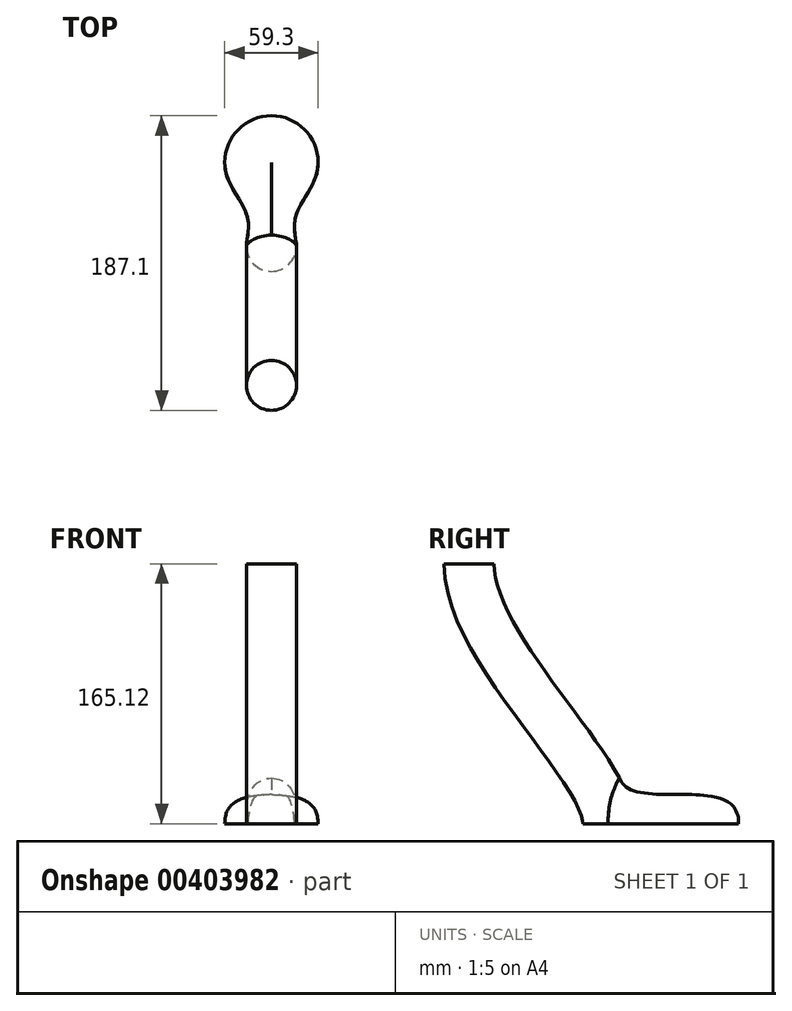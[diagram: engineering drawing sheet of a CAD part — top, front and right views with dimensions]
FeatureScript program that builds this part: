
annotation { "Feature Type Name" : "Feature", "Feature Type Description" : "" }
export const myFeature = defineFeature(function(context is Context, id is Id, definition is map)
    precondition{}
    {
        {
            var Q0;
            Q0=qCreatedBy(makeId("Top.planeOp"),FACE);
            var sketch = newSketch(context, id + "F0", { "sketchPlane" : qUnion([Q0])});
            skArc(sketch, "E0", {"start": v(0, -29.65) * mm, "mid": v(29.65, 0) * mm, "end": v(0, 29.65) * mm});
            skArc(sketch, "E1", {"start": v(0, -64.45) * mm, "mid": v(11.11, -53.34) * mm, "end": v(0, -42.23) * mm});
            skArc(sketch, "E2", {"start": v(0, -69.22) * mm, "mid": v(15.88, -53.34) * mm, "end": v(0, -37.46) * mm});
            skArc(sketch, "E3", {"start": v(0, -15.88) * mm, "mid": v(15.88, 0) * mm, "end": v(0, 15.88) * mm});
            skLineSegment(sketch, "E4", {"start": v(0, 29.65) * mm, "end": v(0, -69.22) * mm});
            skSolve(sketch);
        }
        {
            var Q0;
            Q0=qCreatedBy(makeId("Right.planeOp"),FACE);
            var sketch = newSketch(context, id + "F1", { "sketchPlane" : qUnion([Q0])});
            skLineSegment(sketch, "E5", {"start": v(0, 0) * mm, "end": v(0, 18.54) * mm});
            skPoint(sketch, "E6.0", {"position": v(29.65, 0) * mm});
            skLineSegment(sketch, "E7", {"start": v(0, 0) * mm, "end": v(29.65, 0) * mm});
            skFitSpline(sketch, "E8", {"points": [v(0, 18.54) * mm, v(29.65, 0) * mm], "startDerivative": vector(58.31, -2.04) * mm, "endDerivative": vector(0, -42.4) * mm});
            skLineSegment(sketch, "E9", {"start": v(0, 18.54) * mm, "end": v(-24.67, 19.4) * mm, "construction": true});
            skPoint(sketch, "E10.0", {"position": v(-53.34, 0) * mm});
            skFitSpline(sketch, "E11", {"points": [v(-141.58, 165.12) * mm, v(-53.34, 0) * mm], "startDerivative": vector(0, -164.03) * mm, "endDerivative": vector(0, -107.15) * mm});
            skSolve(sketch);
        }
        {
            var Q0;
            Q0 = qSketchRegion(id + "F1", true);
            var Q1;
            Q1=sQuery(id+"F1.wireOp",EDGE,"E5");
            revolve(context, id + "F2", {"entities" : qUnion([Q0]), "axis" : qUnion([Q1]), "revolveType" : RevolveType.ONE_DIRECTION, "oppositeDirection" : true, "angle" : 90 * degree});
        }
        {
            var Q0;
            {var subQ0=sQuery(id+"F0.wireOp",EDGE,"E1");Q0=makeQuery(id+"F0.imprint","IMPRINT",FACE,{"disambiguationData":[TD([[makeQuery(id+"F0.imprint","IMPRINT",EDGE,{"derivedFrom":subQ0}),-1.0]])]});}
            var Q1;
            {var subQ0=sQuery(id+"F0.wireOp",EDGE,"E1");Q1=makeQuery(id+"F0.imprint","IMPRINT",FACE,{"disambiguationData":[TD([[makeQuery(id+"F0.imprint","IMPRINT",EDGE,{"derivedFrom":subQ0}),1.0]])]});}
            var Q2;
            Q2=sQuery(id+"F1.wireOp",EDGE,"bKoI3nIw-ZmWd-8fnl-qcp9-IL7kywoHTWbe");
            var Q3;
            Q3=sQuery(id+"F1.wireOp",EDGE,"E11");
            sweep(context, id + "F3", {"profiles" : qUnion([Q0, Q1]), "path" : qUnion([Q2, Q3])});
        }
        {
            var Q0;
            Q0=qCreatedBy(makeId("Right.planeOp"),FACE);
            var sketch = newSketch(context, id + "F4", { "sketchPlane" : qUnion([Q0])});
            skPoint(sketch, "E12.0", {"position": v(-53.34, 0) * mm});
            skFitSpline(sketch, "E13", {"points": [v(-53.34, 0) * mm, v(-39.43, 40.04) * mm], "startDerivative": vector(0, 50.47) * mm, "endDerivative": vector(27.1, 40.41) * mm});
            skArc(sketch, "E14", {"start": v(-53.34, 0) * mm, "mid": v(-10.9, 7.7) * mm, "end": v(-39.43, 40.04) * mm});
            skSolve(sketch);
        }
        {
            var Q0;
            Q0 = qSketchRegion(id + "F4", true);
            extrude(context, id + "F5", {"entities" : qUnion([Q0]), "operationType" : NewBodyOperationType.REMOVE, "depth" : 25.4 * mm});
        }
        {
            var Q0;
            Q0=makeQuery(id+"F5.boolean.opBoolean","COPY",FACE,{"derivedFrom":makeQuery(id+"F5.opExtrude","SWEPT_FACE",FACE,{"disambiguationData":[OSD([sQuery(id+"F4.wireOp",EDGE,"E13")])]})});
            var Q1;
            Q1=makeQuery(id+"F2.opRevolve","CAP_FACE",FACE,{"disambiguationData":[OSD([sQuery(id+"F1.wireOp",EDGE,"E5"),sQuery(id+"F1.wireOp",EDGE,"E7"),sQuery(id+"F1.wireOp",EDGE,"E8")])],"isStart":false});
            loft(context, id + "F6", {"startCondition" : LoftEndDerivativeType.MATCH_CURVATURE, "startMagnitude" : 1, "endCondition" : LoftEndDerivativeType.NORMAL_TO_PROFILE, "endMagnitude" : 1, "sheetProfilesArray" : [{ "sheetProfileEntities" : qUnion([Q0]) }, { "sheetProfileEntities" : qUnion([Q1]) }]});
        }
        {
            var Q0;
            Q0=makeQuery(id+"F3.opSweep","SWEPT_BODY",BODY,{"disambiguationData":[OSD([sQuery(id+"F0.wireOp",EDGE,"E2"),sQuery(id+"F0.wireOp",EDGE,"E4"),sQuery(id+"F1.wireOp",EDGE,"E11")])]});
            var Q1;
            Q1=makeQuery(id+"F6.opLoft","SWEPT_BODY",BODY,{"disambiguationData":[OSD([sQuery(id+"F1.wireOp",EDGE,"E5"),sQuery(id+"F1.wireOp",EDGE,"E7"),sQuery(id+"F1.wireOp",EDGE,"E8"),sQuery(id+"F4.wireOp",EDGE,"E13")])]});
            var Q2;
            Q2=makeQuery(id+"F2.opRevolve","SWEPT_BODY",BODY,{"disambiguationData":[OSD([sQuery(id+"F1.wireOp",EDGE,"E5"),sQuery(id+"F1.wireOp",EDGE,"E7"),sQuery(id+"F1.wireOp",EDGE,"E8")])]});
            booleanBodies(context, id + "F7", {"operationType" : BooleanOperationType.UNION, "tools" : qUnion([Q0, Q1, Q2])});
        }
        {
            var Q0;
            Q0=makeQuery(id+"F3.opSweep","SWEPT_BODY",BODY,{"disambiguationData":[OSD([sQuery(id+"F0.wireOp",EDGE,"E2"),sQuery(id+"F0.wireOp",EDGE,"E4"),sQuery(id+"F1.wireOp",EDGE,"E11")])]});
            var Q1;
            {var subQ0=sQuery(id+"F4.wireOp",EDGE,"E13");var subQ1=sQuery(id+"F1.wireOp",EDGE,"E11");var subQ2=sQuery(id+"F0.wireOp",EDGE,"E2");var subQ3=sQuery(id+"F4.wireOp",EDGE,"E14");var subQ4=sQuery(id+"F1.wireOp",EDGE,"E5");var subQ5=sQuery(id+"F1.wireOp",EDGE,"E8");var subQ6=sQuery(id+"F1.wireOp",EDGE,"E7");Q1=makeQuery(id+"F7.opBoolean","MERGE",FACE,{"derivedFrom":[makeQuery(id+"F2.opRevolve","CAP_FACE",FACE,{"disambiguationData":[OSD([subQ4,subQ6,subQ5])],"isStart":true}),makeQuery(id+"F3.opSweep","SWEPT_FACE",FACE,{"disambiguationData":[OSD([sQuery(id+"F0.wireOp",EDGE,"E4"),subQ1])]}),makeQuery(id+"F6.opLoft","SWEPT_FACE",FACE,{"disambiguationData":[OSD([subQ2,subQ4,subQ6,subQ5,subQ1,subQ0,subQ3]),TDD([makeQuery(id+"F2.opRevolve","CAP_VERTEX",VERTEX,{"disambiguationData":[OSD([subQ4,subQ6])],"isStart":true}),makeQuery(id+"F2.opRevolve","CAP_VERTEX",VERTEX,{"disambiguationData":[OSD([subQ4,subQ5])],"isStart":true}),makeQuery(id+"F2.opRevolve","CAP_EDGE",EDGE,{"disambiguationData":[OSD([subQ4])],"isStart":true}),makeQuery(id+"F5.boolean.opBoolean","COPY",VERTEX,{"derivedFrom":makeQuery(id+"F5.opExtrude","CAP_VERTEX",VERTEX,{"disambiguationData":[OSD([subQ0,subQ3]),TDD([makeQuery(id+"F4.imprint","INTERSECT",VERTEX,{"disambiguationData":[OD(0.0)],"derivedFrom":[subQ0,subQ3]})])],"isStart":true})}),makeQuery(id+"F5.boolean.opBoolean","INTERSECT",VERTEX,{"disambiguationData":[OD(1.0)],"derivedFrom":[makeQuery(id+"F3.opSweep","SWEPT_FACE",FACE,{"disambiguationData":[OSD([subQ2,subQ1])]}),makeQuery(id+"F5.opExtrude","SWEPT_FACE",FACE,{"disambiguationData":[OSD([subQ0])]})]}),makeQuery(id+"F5.boolean.opBoolean","COPY",EDGE,{"derivedFrom":makeQuery(id+"F5.opExtrude","CAP_EDGE",EDGE,{"disambiguationData":[OSD([subQ0])],"isStart":true})})])]})]});}
            mirror(context, id + "F8", {"operationType" : NewBodyOperationType.ADD, "entities" : qUnion([Q0]), "mirrorPlane" : qUnion([Q1])});
        }
    });
